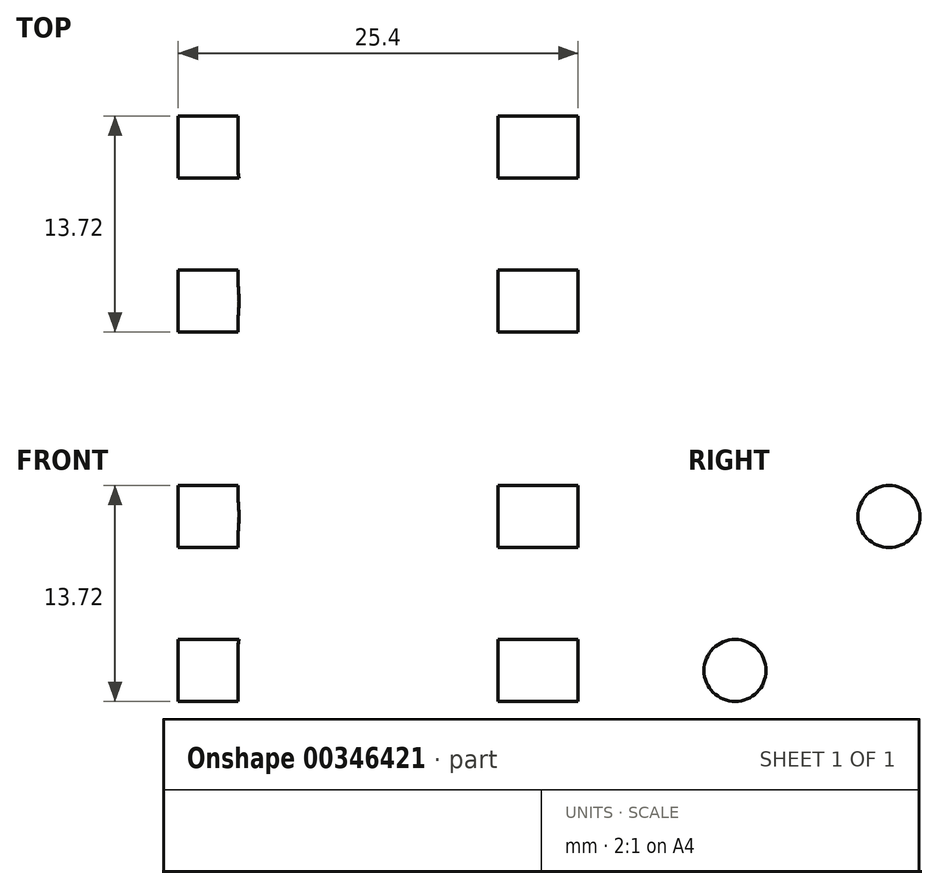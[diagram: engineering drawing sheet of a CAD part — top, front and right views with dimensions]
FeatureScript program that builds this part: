
annotation { "Feature Type Name" : "Feature", "Feature Type Description" : "" }
export const myFeature = defineFeature(function(context is Context, id is Id, definition is map)
    precondition{}
    {
        {
            var Q0;
            Q0=qCreatedBy(makeId("Front.planeOp"),FACE);
            var sketch = newSketch(context, id + "F0", { "sketchPlane" : qUnion([Q0])});
            skLineSegment(sketch, "E0.top", {"start": v(-33.09, 16.91) * mm, "end": v(-7.69, 16.91) * mm});
            skLineSegment(sketch, "E0.left", {"start": v(-33.09, 33.42) * mm, "end": v(-33.09, 16.91) * mm});
            skLineSegment(sketch, "E0.right", {"start": v(-7.69, 33.42) * mm, "end": v(-7.69, 16.91) * mm});
            skPoint(sketch, "E1.visualSharp", {"position": v(-29.28, 23.26) * mm});
            skLineSegment(sketch, "E2", {"start": v(-33.09, 33.42) * mm, "end": v(-31.18, 33.42) * mm});
            skLineSegment(sketch, "E3", {"start": v(-29.28, 31.52) * mm, "end": v(-29.28, 25.17) * mm});
            skLineSegment(sketch, "E4", {"start": v(-7.69, 33.42) * mm, "end": v(-14.67, 33.42) * mm});
            skLineSegment(sketch, "E5", {"start": v(-16.58, 31.52) * mm, "end": v(-16.58, 25.17) * mm});
            skLineSegment(sketch, "E6", {"start": v(-27.37, 23.26) * mm, "end": v(-18.48, 23.26) * mm});
            skPoint(sketch, "E7.visualSharp", {"position": v(-16.58, 33.42) * mm});
            skArc(sketch, "E7.filletArc", {"start": v(-14.67, 33.42) * mm, "mid": v(-16.02, 32.86) * mm, "end": v(-16.58, 31.52) * mm});
            skPoint(sketch, "E8.visualSharp", {"position": v(-16.58, 23.26) * mm});
            skArc(sketch, "E8.filletArc", {"start": v(-18.48, 23.26) * mm, "mid": v(-17.13, 23.82) * mm, "end": v(-16.58, 25.17) * mm});
            skArc(sketch, "E9.filletArc", {"start": v(-29.28, 25.17) * mm, "mid": v(-28.72, 23.82) * mm, "end": v(-27.37, 23.26) * mm});
            skPoint(sketch, "E10.visualSharp", {"position": v(-29.28, 33.42) * mm});
            skArc(sketch, "E10.filletArc", {"start": v(-29.28, 31.52) * mm, "mid": v(-29.83, 32.86) * mm, "end": v(-31.18, 33.42) * mm});
            skSolve(sketch);
        }
        {
            var Q0;
            Q0=makeQuery(id+"F0.imprint","IMPRINT",FACE,{"disambiguationData":[TD([[makeQuery(id+"F0.imprint","IMPRINT",EDGE,{"derivedFrom":sQuery(id+"F0.wireOp",EDGE,"E0.top")}),1.0]])]});
            var Q1;
            Q1=sQuery(id+"F0.wireOp",EDGE,"E0.top");
            revolve(context, id + "F1", {"entities" : qUnion([Q0]), "axis" : qUnion([Q1]), "revolveType" : RevolveType.FULL});
        }
        {
            var Q0;
            Q0=makeQuery(id+"F1.opRevolve","SWEPT_FACE",FACE,{"disambiguationData":[OSD([sQuery(id+"F0.wireOp",EDGE,"E0.right")])]});
            var sketch = newSketch(context, id + "F2", { "sketchPlane" : qUnion([Q0])});
            skCircle(sketch, "E11", {"center": v(0, 16.91) * mm, "radius": 9.78 * mm});
            skCircle(sketch, "E12", {"center": v(9.78, 16.91) * mm, "radius": 1.97 * mm});
            skCircle(sketch, "E13.1.0", {"center": v(6.91, 23.83) * mm, "radius": 1.97 * mm});
            skCircle(sketch, "E13.2.0", {"center": v(0, 26.7) * mm, "radius": 1.97 * mm});
            skCircle(sketch, "E13.3.0", {"center": v(-6.91, 23.83) * mm, "radius": 1.97 * mm});
            skCircle(sketch, "E13.4.0", {"center": v(-9.78, 16.91) * mm, "radius": 1.97 * mm});
            skCircle(sketch, "E13.5.0", {"center": v(-6.91, 10) * mm, "radius": 1.97 * mm});
            skCircle(sketch, "E13.6.0", {"center": v(0, 7.13) * mm, "radius": 1.97 * mm});
            skCircle(sketch, "E13.7.0", {"center": v(6.91, 10) * mm, "radius": 1.97 * mm});
            skCircle(sketch, "E14", {"center": v(0, 16.91) * mm, "radius": 3.18 * mm});
            skSolve(sketch);
        }
        {
            var Q0;
            {var subQ0=sQuery(id+"F2.wireOp",EDGE,"E13.1.0");var subQ1=sQuery(id+"F2.wireOp",EDGE,"E11");var subQ2=makeQuery(id+"F2.imprint","INTERSECT",VERTEX,{"disambiguationData":[OD(0.0)],"derivedFrom":[subQ1,subQ0]});Q0=makeQuery(id+"F2.imprint","IMPRINT",FACE,{"disambiguationData":[TD([[makeQuery(id+"F2.imprint","IMPRINT",EDGE,{"disambiguationData":[TD([[subQ2,-1.0]])],"derivedFrom":subQ1}),1.0]])]});}
            var Q1;
            {var subQ0=sQuery(id+"F2.wireOp",EDGE,"E13.1.0");var subQ1=sQuery(id+"F2.wireOp",EDGE,"E11");var subQ2=makeQuery(id+"F2.imprint","INTERSECT",VERTEX,{"disambiguationData":[OD(0.0)],"derivedFrom":[subQ1,subQ0]});Q1=makeQuery(id+"F2.imprint","IMPRINT",FACE,{"disambiguationData":[TD([[makeQuery(id+"F2.imprint","IMPRINT",EDGE,{"disambiguationData":[TD([[subQ2,-1.0]])],"derivedFrom":subQ1}),-1.0]])]});}
            var Q2;
            {var subQ0=sQuery(id+"F2.wireOp",EDGE,"E13.2.0");var subQ1=sQuery(id+"F2.wireOp",EDGE,"E11");var subQ2=makeQuery(id+"F2.imprint","INTERSECT",VERTEX,{"disambiguationData":[OD(0.0)],"derivedFrom":[subQ1,subQ0]});Q2=makeQuery(id+"F2.imprint","IMPRINT",FACE,{"disambiguationData":[TD([[makeQuery(id+"F2.imprint","IMPRINT",EDGE,{"disambiguationData":[TD([[subQ2,-1.0]])],"derivedFrom":subQ1}),1.0]])]});}
            var Q3;
            {var subQ0=sQuery(id+"F2.wireOp",EDGE,"E13.2.0");var subQ1=sQuery(id+"F2.wireOp",EDGE,"E11");var subQ2=makeQuery(id+"F2.imprint","INTERSECT",VERTEX,{"disambiguationData":[OD(0.0)],"derivedFrom":[subQ1,subQ0]});Q3=makeQuery(id+"F2.imprint","IMPRINT",FACE,{"disambiguationData":[TD([[makeQuery(id+"F2.imprint","IMPRINT",EDGE,{"disambiguationData":[TD([[subQ2,-1.0]])],"derivedFrom":subQ1}),-1.0]])]});}
            var Q4;
            {var subQ0=sQuery(id+"F2.wireOp",EDGE,"E13.3.0");var subQ1=sQuery(id+"F2.wireOp",EDGE,"E11");var subQ2=makeQuery(id+"F2.imprint","INTERSECT",VERTEX,{"disambiguationData":[OD(0.0)],"derivedFrom":[subQ1,subQ0]});Q4=makeQuery(id+"F2.imprint","IMPRINT",FACE,{"disambiguationData":[TD([[makeQuery(id+"F2.imprint","IMPRINT",EDGE,{"disambiguationData":[TD([[subQ2,-1.0]])],"derivedFrom":subQ1}),1.0]])]});}
            var Q5;
            {var subQ0=sQuery(id+"F2.wireOp",EDGE,"E13.3.0");var subQ1=sQuery(id+"F2.wireOp",EDGE,"E11");var subQ2=makeQuery(id+"F2.imprint","INTERSECT",VERTEX,{"disambiguationData":[OD(0.0)],"derivedFrom":[subQ1,subQ0]});Q5=makeQuery(id+"F2.imprint","IMPRINT",FACE,{"disambiguationData":[TD([[makeQuery(id+"F2.imprint","IMPRINT",EDGE,{"disambiguationData":[TD([[subQ2,-1.0]])],"derivedFrom":subQ1}),-1.0]])]});}
            var Q6;
            {var subQ0=sQuery(id+"F2.wireOp",EDGE,"E13.4.0");var subQ1=sQuery(id+"F2.wireOp",EDGE,"E11");var subQ2=makeQuery(id+"F2.imprint","INTERSECT",VERTEX,{"disambiguationData":[OD(0.0)],"derivedFrom":[subQ1,subQ0]});Q6=makeQuery(id+"F2.imprint","IMPRINT",FACE,{"disambiguationData":[TD([[makeQuery(id+"F2.imprint","IMPRINT",EDGE,{"disambiguationData":[TD([[subQ2,-1.0]])],"derivedFrom":subQ1}),1.0]])]});}
            var Q7;
            {var subQ0=sQuery(id+"F2.wireOp",EDGE,"E13.4.0");var subQ1=sQuery(id+"F2.wireOp",EDGE,"E11");var subQ2=makeQuery(id+"F2.imprint","INTERSECT",VERTEX,{"disambiguationData":[OD(0.0)],"derivedFrom":[subQ1,subQ0]});Q7=makeQuery(id+"F2.imprint","IMPRINT",FACE,{"disambiguationData":[TD([[makeQuery(id+"F2.imprint","IMPRINT",EDGE,{"disambiguationData":[TD([[subQ2,-1.0]])],"derivedFrom":subQ1}),-1.0]])]});}
            var Q8;
            {var subQ0=sQuery(id+"F2.wireOp",EDGE,"E13.5.0");var subQ1=sQuery(id+"F2.wireOp",EDGE,"E11");var subQ2=makeQuery(id+"F2.imprint","INTERSECT",VERTEX,{"disambiguationData":[OD(0.0)],"derivedFrom":[subQ1,subQ0]});Q8=makeQuery(id+"F2.imprint","IMPRINT",FACE,{"disambiguationData":[TD([[makeQuery(id+"F2.imprint","IMPRINT",EDGE,{"disambiguationData":[TD([[subQ2,-1.0]])],"derivedFrom":subQ1}),1.0]])]});}
            var Q9;
            {var subQ0=sQuery(id+"F2.wireOp",EDGE,"E13.5.0");var subQ1=sQuery(id+"F2.wireOp",EDGE,"E11");var subQ2=makeQuery(id+"F2.imprint","INTERSECT",VERTEX,{"disambiguationData":[OD(0.0)],"derivedFrom":[subQ1,subQ0]});Q9=makeQuery(id+"F2.imprint","IMPRINT",FACE,{"disambiguationData":[TD([[makeQuery(id+"F2.imprint","IMPRINT",EDGE,{"disambiguationData":[TD([[subQ2,-1.0]])],"derivedFrom":subQ1}),-1.0]])]});}
            var Q10;
            {var subQ0=sQuery(id+"F2.wireOp",EDGE,"E13.6.0");var subQ1=sQuery(id+"F2.wireOp",EDGE,"E11");var subQ2=makeQuery(id+"F2.imprint","INTERSECT",VERTEX,{"disambiguationData":[OD(0.0)],"derivedFrom":[subQ1,subQ0]});Q10=makeQuery(id+"F2.imprint","IMPRINT",FACE,{"disambiguationData":[TD([[makeQuery(id+"F2.imprint","IMPRINT",EDGE,{"disambiguationData":[TD([[subQ2,-1.0]])],"derivedFrom":subQ1}),1.0]])]});}
            var Q11;
            {var subQ0=sQuery(id+"F2.wireOp",EDGE,"E13.6.0");var subQ1=sQuery(id+"F2.wireOp",EDGE,"E11");var subQ2=makeQuery(id+"F2.imprint","INTERSECT",VERTEX,{"disambiguationData":[OD(0.0)],"derivedFrom":[subQ1,subQ0]});Q11=makeQuery(id+"F2.imprint","IMPRINT",FACE,{"disambiguationData":[TD([[makeQuery(id+"F2.imprint","IMPRINT",EDGE,{"disambiguationData":[TD([[subQ2,-1.0]])],"derivedFrom":subQ1}),-1.0]])]});}
            var Q12;
            {var subQ0=sQuery(id+"F2.wireOp",EDGE,"E13.7.0");var subQ1=sQuery(id+"F2.wireOp",EDGE,"E11");var subQ2=makeQuery(id+"F2.imprint","INTERSECT",VERTEX,{"disambiguationData":[OD(0.0)],"derivedFrom":[subQ1,subQ0]});Q12=makeQuery(id+"F2.imprint","IMPRINT",FACE,{"disambiguationData":[TD([[makeQuery(id+"F2.imprint","IMPRINT",EDGE,{"disambiguationData":[TD([[subQ2,-1.0]])],"derivedFrom":subQ1}),1.0]])]});}
            var Q13;
            {var subQ0=sQuery(id+"F2.wireOp",EDGE,"E13.7.0");var subQ1=sQuery(id+"F2.wireOp",EDGE,"E11");var subQ2=makeQuery(id+"F2.imprint","INTERSECT",VERTEX,{"disambiguationData":[OD(0.0)],"derivedFrom":[subQ1,subQ0]});Q13=makeQuery(id+"F2.imprint","IMPRINT",FACE,{"disambiguationData":[TD([[makeQuery(id+"F2.imprint","IMPRINT",EDGE,{"disambiguationData":[TD([[subQ2,-1.0]])],"derivedFrom":subQ1}),-1.0]])]});}
            var Q14;
            {var subQ0=sQuery(id+"F2.wireOp",EDGE,"E12");var subQ1=sQuery(id+"F2.wireOp",EDGE,"E11");var subQ2=makeQuery(id+"F2.imprint","INTERSECT",VERTEX,{"disambiguationData":[OD(0.0)],"derivedFrom":[subQ1,subQ0]});Q14=makeQuery(id+"F2.imprint","IMPRINT",FACE,{"disambiguationData":[TD([[makeQuery(id+"F2.imprint","IMPRINT",EDGE,{"disambiguationData":[TD([[subQ2,1.0]])],"derivedFrom":subQ1}),1.0]])]});}
            var Q15;
            {var subQ0=sQuery(id+"F2.wireOp",EDGE,"E12");var subQ1=sQuery(id+"F2.wireOp",EDGE,"E11");var subQ2=makeQuery(id+"F2.imprint","INTERSECT",VERTEX,{"disambiguationData":[OD(0.0)],"derivedFrom":[subQ1,subQ0]});Q15=makeQuery(id+"F2.imprint","IMPRINT",FACE,{"disambiguationData":[TD([[makeQuery(id+"F2.imprint","IMPRINT",EDGE,{"disambiguationData":[TD([[subQ2,1.0]])],"derivedFrom":subQ1}),-1.0]])]});}
            var Q16;
            Q16=makeQuery(id+"F2.imprint","IMPRINT",FACE,{"disambiguationData":[TD([[makeQuery(id+"F2.imprint","IMPRINT",EDGE,{"derivedFrom":sQuery(id+"F2.wireOp",EDGE,"E14")}),1.0]])]});
            extrude(context, id + "F3", {"entities" : qUnion([Q0, Q1, Q2, Q3, Q4, Q5, Q6, Q7, Q8, Q9, Q10, Q11, Q12, Q13, Q14, Q15, Q16]), "operationType" : NewBodyOperationType.REMOVE, "oppositeDirection" : true, "depth" : 25.4 * mm});
        }
        {
            var Q0;
            Q0=makeQuery(id+"F1.opRevolve","SWEPT_FACE",FACE,{"disambiguationData":[OSD([sQuery(id+"F0.wireOp",EDGE,"E5")])]});
            var sketch = newSketch(context, id + "F4", { "sketchPlane" : qUnion([Q0])});
            skCircle(sketch, "E15", {"center": v(-9.78, 16.91) * mm, "radius": 3.05 * mm});
            skCircle(sketch, "E16.1.0", {"center": v(-6.91, 10) * mm, "radius": 3.05 * mm});
            skCircle(sketch, "E16.2.0", {"center": v(0, 7.13) * mm, "radius": 3.05 * mm});
            skCircle(sketch, "E16.3.0", {"center": v(6.91, 10) * mm, "radius": 3.05 * mm});
            skCircle(sketch, "E16.4.0", {"center": v(9.78, 16.91) * mm, "radius": 3.05 * mm});
            skCircle(sketch, "E16.5.0", {"center": v(6.91, 23.83) * mm, "radius": 3.05 * mm});
            skCircle(sketch, "E16.6.0", {"center": v(0, 26.7) * mm, "radius": 3.05 * mm});
            skCircle(sketch, "E16.7.0", {"center": v(-6.91, 23.83) * mm, "radius": 3.05 * mm});
            skPoint(sketch, "E16.center", {"position": v(0, 16.91) * mm});
            skSolve(sketch);
        }
        {
            var Q0;
            Q0 = qSketchRegion(id + "F4", true);
            extrude(context, id + "F5", {"entities" : qUnion([Q0]), "operationType" : NewBodyOperationType.REMOVE, "oppositeDirection" : true, "depth" : 3.8 * mm, "hasSecondDirection" : true, "secondDirectionOppositeDirection" : false, "secondDirectionDepth" : 1.9 * mm});
        }
        {
            var Q0;
            Q0=qCreatedBy(makeId("Front.planeOp"),FACE);
            cPlane(context, id + "F6", {"entities" : qUnion([Q0]), "cplaneType" : CPlaneType.OFFSET, "offset" : 6.35 * mm, "width" : 152.4 * mm, "height" : 152.4 * mm});
        }
        {
            var Q0;
            Q0=qCreatedBy(id+"F6.planeOp",FACE);
            var sketch = newSketch(context, id + "F7", { "sketchPlane" : qUnion([Q0])});
            skLineSegment(sketch, "E17.0", {"start": v(-27.37, 10.56) * mm, "end": v(-27.37, 23.26) * mm});
            skLineSegment(sketch, "E17.1", {"start": v(-18.48, 10.56) * mm, "end": v(-18.48, 23.26) * mm});
            skLineSegment(sketch, "E18", {"start": v(-27.37, 17.76) * mm, "end": v(-18.48, 17.76) * mm});
            skCircle(sketch, "E19", {"center": v(-22.93, 17.76) * mm, "radius": 1.2 * mm});
            skSolve(sketch);
        }
        {
            var Q0;
            Q0 = qSketchRegion(id + "F7", true);
            extrude(context, id + "F8", {"entities" : qUnion([Q0]), "operationType" : NewBodyOperationType.REMOVE, "oppositeDirection" : true, "depth" : 25.4 * mm});
        }
    });
